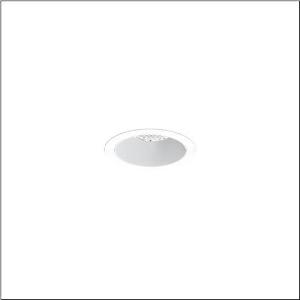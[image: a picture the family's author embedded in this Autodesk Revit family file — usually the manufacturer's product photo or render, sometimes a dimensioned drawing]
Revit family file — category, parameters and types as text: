
# Revit family: lunis_21_m_51db18tc91c
name_source: partatom
category: Lighting Fixtures
units: mm (PartAtom-declared; Revit-internal decimal feet)

## family parameters
Cut with Voids When Loaded = No
Host = Face
Light Source = No
Part Type = Normal
Room Calculation Point = No
Round Connector Dimension = Use Diameter
Shared = No

## types (1)
- --- (1 x LED, 3910 lm, 26 W, 4000K)
    Apparent Load = 26 VA
    CIE Flux Codes = 95 100 100 100 100
    Color Rendering = 80
    Color Temperature = 4000K
    Default Elevation = 1800 mm
    Description = Lunis 21,  M, downlight, light control with lens, of PMMA, anti glare with reflector, of aluminium, light emission: direct distribution, LED rated luminous flux: 1.800lm, light colour: 8tw, with terminal, 5-pole, mains connection: 220..240V, AC/DC, 0/50..60Hz, housing, round, of diecast aluminium, traffic white (RAL 9016), diameter: 115mm, clamping range: 1..40mm, protection rating (complete): IP20, protection rating (on room side): IP54, insulation class (complete): insulation class II (safety insulation), certification: CE, impact resistance: IK03, packaging unit: 1 piece
    Height = 0 mm  [stored 0 ft]
    Lamp = 1 x LED
    Lamp Light Flux = 3910 lm
    Lamp Power = 26 W
    Lamp count = 1
    Length = 115 mm
    Luminous efficacy = 150 lm/W
    Manufacturer = Siteco
    ModVariant = No
    Model = 51DB18TC91C
    Mounting Place = Ceiling
    Mounting Type = Recessed
    Number of Poles = 1
    OnlyDefault = Yes
    Power Factor = 1
    Product Name = Lunis 21 M
    Product group = downlight
    ProductGroupID = 400
    Protection Class = Protection class II
    Protection Degree = IP 20
    RLX_Detail_Level = 1
    RLX_Emergency_Light_Flux = 0 lm
    RLX_Emergency_Type = 0
    RLX_Emergency_Type_DB = No
    RlxData = <blob elided: 10425 chars, md5=20fd3a77>
    Socket = socket
    Standby Power = 0 W
    System Light Flux = 3910 lm
    System Power = 26 W
    Type Comments = individual setting: colour temperature 4000K, luminous flux: 100 % | (ON | ON | OFF | OFF) | 700 mA
    Type Image = l_1290852.jpg
    URL = http://relux.com
    VarID = @adj_017567
    Voltage = 0 V
    Weight = 0.00 kg
    Width = 0 mm  [stored 0 ft]

note: [stored X ft] marks values corroborated as IEEE doubles in the binary element streams (Revit-internal decimal feet)

## geometry (parser evidence)
native form markers: Sweep x10
no freeform markers — native parametric forms only
